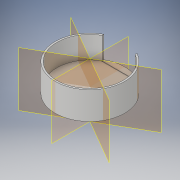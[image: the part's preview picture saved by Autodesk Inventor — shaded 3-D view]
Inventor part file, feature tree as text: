
AUTODESK INVENTOR PART (.ipt)
format: ipt  version: 2019 (Build 230136000, 136)  size: 404,480 bytes
history: native  units: mm
features: sketch x6, extrude x5, plane x5, fillet x4, loft x2, other x2
ambient origin geometry x8: Origin, YZ Plane, XZ Plane, XY Plane, X Axis, Y Axis, Z Axis, Center Point
bodies: Solid1 (feature_tree)
feature tree (24):
  extrude  "Extrusion1"  Depth=126.0mm
  extrude  "Extrusion2"  Depth=1.0mm
  extrude  "Extrusion3"  Depth=60.0mm
  plane  "Work Plane2"
  plane  "Work Plane3"
  extrude  "Extrusion6"  Depth=10.0mm TaperAngle=0.0deg
  loft  "Loft3"
  extrude  "Extrusion7"  Depth=20.0mm TaperAngle=0.0deg
  loft  "Loft4"
  fillet  "Fillet5"  Radius=126.0mm
  fillet  "Fillet6"  [1 undecoded]
  fillet  "Fillet7"  [1 undecoded]
  fillet  "Fillet8"  [1 undecoded]
  plane  "Work Plane6"
  sketch  "Sketch1"  dims[d0=120.0mm d1=126.0mm]
  sketch  "Sketch2"  dims[d2=40.0mm d3=0.0mm d4=1.0mm]
  sketch  "Sketch3"  dims[d5=1.0mm d6=60.0mm]
  sketch  "Sketch11"  dims[d7=120.0mm d8=10.0mm d9=0.0mm]
  sketch  "Sketch12"  dims[d10=10.0mm d11=0.0mm d21=40.0mm]
  sketch  "Sketch13"  dims[d27=20.0mm d28=20.0mm d29=0.0mm d36=126.0mm d37=126.0mm d43=120.0deg d45=0.0mm d46=90.0deg d47=0.0mm d48=90.0deg d49=20.0mm d50=0.0mm d51=0.0mm d52=90.0deg d53=0.0mm d54=90.0deg d56=4.0mm d57=4.0mm d58=4.0mm d59=4.0mm]
  other  "Edges3"
  other  "Edges4"
  plane  "Work Plane4"
  plane  "Work Plane5"
note: 3 required parameter values undecoded (feature->parameter linkage not recoverable at this tier; creation-order binding heuristic only, values carry confidence <= 0.55)
